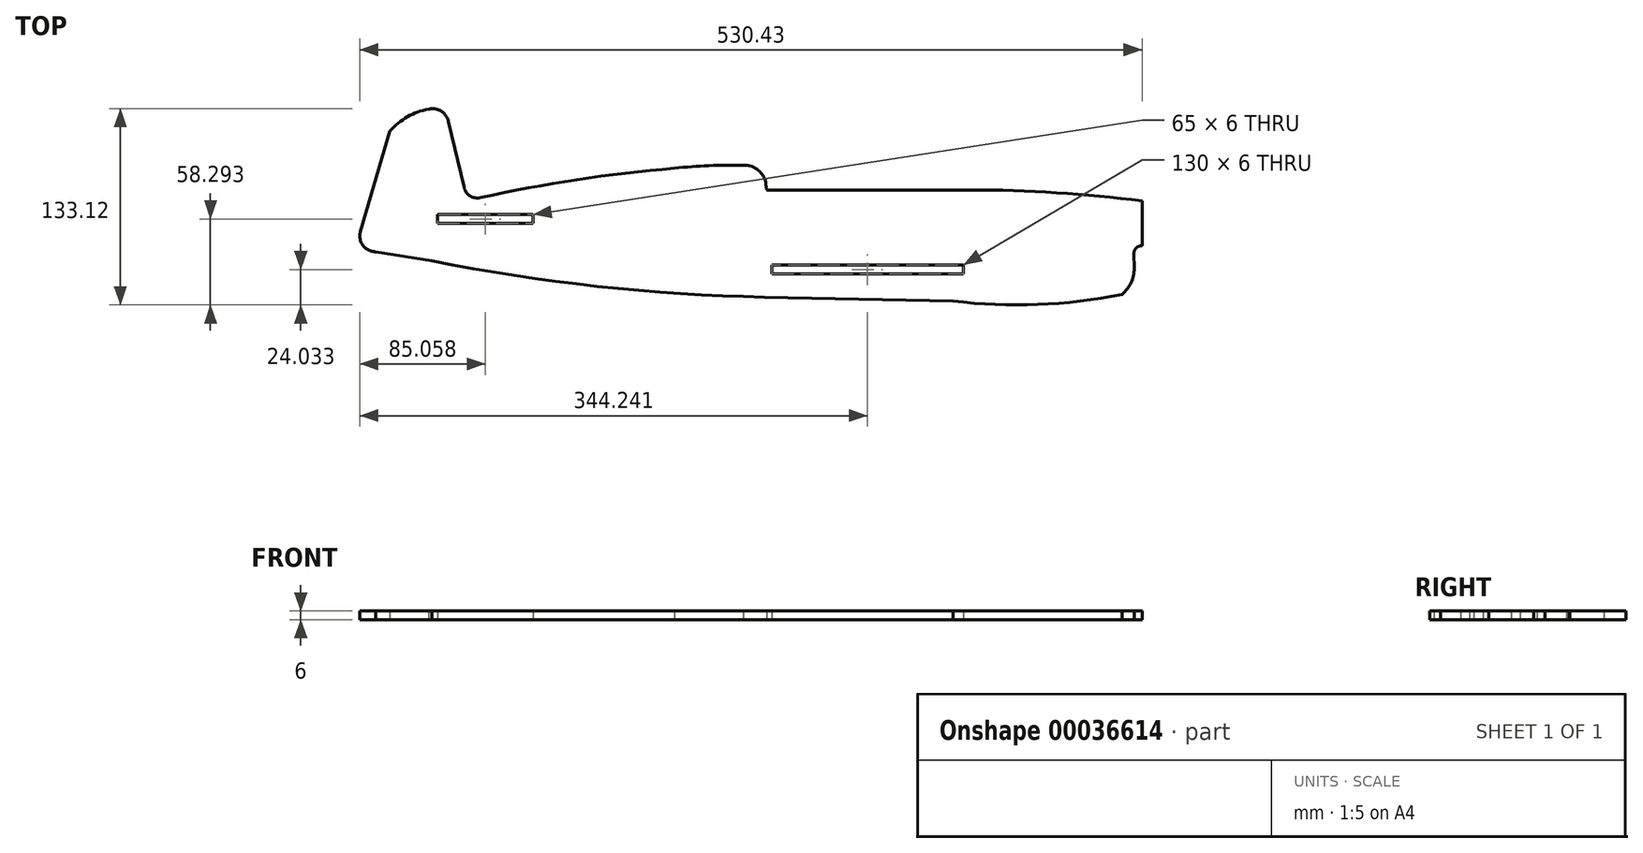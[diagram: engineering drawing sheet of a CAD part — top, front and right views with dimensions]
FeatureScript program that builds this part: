
annotation { "Feature Type Name" : "Feature", "Feature Type Description" : "" }
export const myFeature = defineFeature(function(context is Context, id is Id, definition is map)
    precondition{}
    {
        {
            var Q0;
            Q0=qCreatedBy(makeId("Top.planeOp"),FACE);
            var sketch = newSketch(context, id + "F0", { "sketchPlane" : qUnion([Q0])});
            skLineSegment(sketch, "E0", {"start": v(-183.54, 68.38) * mm, "end": v(-172.91, 23.37) * mm});
            skLineSegment(sketch, "E1", {"start": v(-223.12, 61.67) * mm, "end": v(-243.16, -6.62) * mm});
            skArc(sketch, "E2", {"start": v(-196.86, 76.5) * mm, "mid": v(-211.28, 71.36) * mm, "end": v(-223.12, 61.67) * mm});
            skArc(sketch, "E3", {"start": v(-183.54, 68.38) * mm, "mid": v(-188.5, 75.23) * mm, "end": v(-196.86, 76.5) * mm});
            skArc(sketch, "E4", {"start": v(-30.24, 36.43) * mm, "mid": v(-96.43, 28.65) * mm, "end": v(-161.95, 16.47) * mm});
            skArc(sketch, "E5", {"start": v(-172.91, 23.37) * mm, "mid": v(-168.84, 17.68) * mm, "end": v(-161.95, 16.47) * mm});
            skArc(sketch, "E6", {"start": v(16.5, 38.37) * mm, "mid": v(-6.9, 38.18) * mm, "end": v(-30.24, 36.43) * mm});
            skArc(sketch, "E7", {"start": v(31.8, 25.63) * mm, "mid": v(26.71, 35.07) * mm, "end": v(16.5, 38.37) * mm});
            skLineSegment(sketch, "E8", {"start": v(31.8, 25.63) * mm, "end": v(32.24, 21.7) * mm});
            skLineSegment(sketch, "E9", {"start": v(32.24, 21.7) * mm, "end": v(170.61, 21.7) * mm});
            skArc(sketch, "E10", {"start": v(286.84, 14.21) * mm, "mid": v(228.85, 19.83) * mm, "end": v(170.61, 21.7) * mm});
            skArc(sketch, "E11", {"start": v(-194.83, -26.36) * mm, "mid": v(-82.6, -43.65) * mm, "end": v(30.73, -51) * mm});
            skLineSegment(sketch, "E12", {"start": v(-194.83, -26.36) * mm, "end": v(-232.8, -20.18) * mm});
            skArc(sketch, "E13", {"start": v(-243.16, -6.62) * mm, "mid": v(-241.41, -16.03) * mm, "end": v(-232.8, -20.18) * mm});
            skLineSegment(sketch, "E14", {"start": v(30.73, -51) * mm, "end": v(158.6, -53.64) * mm});
            skArc(sketch, "E15", {"start": v(158.6, -53.64) * mm, "mid": v(216.07, -56) * mm, "end": v(273.17, -49.1) * mm});
            skArc(sketch, "E16", {"start": v(273.17, -49.1) * mm, "mid": v(279.34, -41.28) * mm, "end": v(281.46, -31.55) * mm});
            skLineSegment(sketch, "E17", {"start": v(281.46, -31.55) * mm, "end": v(281.33, -21.32) * mm});
            skLineSegment(sketch, "E18", {"start": v(286.84, 14.21) * mm, "end": v(286.84, -16.2) * mm});
            skArc(sketch, "E19", {"start": v(286.84, -16.2) * mm, "mid": v(282.95, -17.54) * mm, "end": v(281.33, -21.32) * mm});
            skLineSegment(sketch, "E20.bottom", {"start": v(-191.03, 5) * mm, "end": v(-126.03, 5) * mm});
            skLineSegment(sketch, "E20.top", {"start": v(-191.03, -1) * mm, "end": v(-126.03, -1) * mm});
            skLineSegment(sketch, "E20.left", {"start": v(-191.03, 5) * mm, "end": v(-191.03, -1) * mm});
            skLineSegment(sketch, "E20.right", {"start": v(-126.03, 5) * mm, "end": v(-126.03, -1) * mm});
            skLineSegment(sketch, "E21", {"start": v(-243.16, -6.62) * mm, "end": v(286.84, -6.62) * mm});
            skLineSegment(sketch, "E22.bottom", {"start": v(35.65, -29.26) * mm, "end": v(165.65, -29.26) * mm});
            skLineSegment(sketch, "E22.top", {"start": v(35.65, -35.26) * mm, "end": v(165.65, -35.26) * mm});
            skLineSegment(sketch, "E22.left", {"start": v(35.65, -29.26) * mm, "end": v(35.65, -35.26) * mm});
            skLineSegment(sketch, "E22.right", {"start": v(165.65, -29.26) * mm, "end": v(165.65, -35.26) * mm});
            skSolve(sketch);
        }
        {
            var Q0;
            Q0=makeQuery(id+"F0.imprint","IMPRINT",FACE,{"disambiguationData":[TD([[makeQuery(id+"F0.imprint","IMPRINT",EDGE,{"derivedFrom":sQuery(id+"F0.wireOp",EDGE,"E0")}),-1.0]])]});
            var Q1;
            Q1=makeQuery(id+"F0.imprint","IMPRINT",FACE,{"disambiguationData":[TD([[makeQuery(id+"F0.imprint","IMPRINT",EDGE,{"derivedFrom":sQuery(id+"F0.wireOp",EDGE,"E11")}),1.0]])]});
            extrude(context, id + "F1", {"entities" : qUnion([Q0, Q1]), "depth" : 6 * mm});
        }
    });
